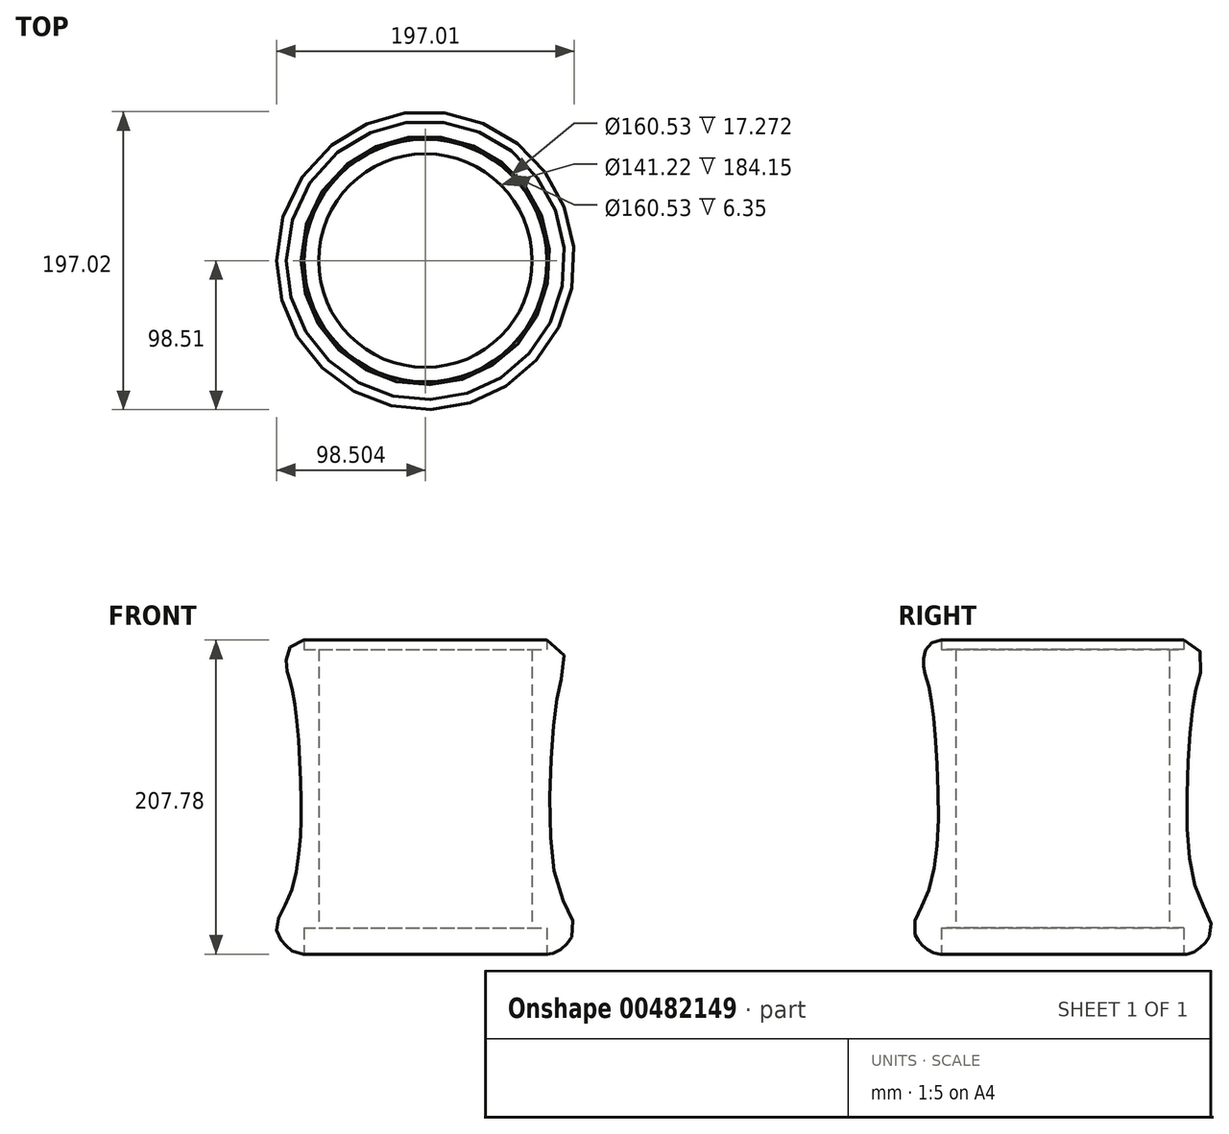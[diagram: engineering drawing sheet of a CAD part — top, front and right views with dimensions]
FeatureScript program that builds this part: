
annotation { "Feature Type Name" : "Feature", "Feature Type Description" : "" }
export const myFeature = defineFeature(function(context is Context, id is Id, definition is map)
    precondition{}
    {
        {
            var Q0;
            Q0=qCreatedBy(makeId("Front.planeOp"),FACE);
            var sketch = newSketch(context, id + "F0", { "sketchPlane" : qUnion([Q0])});
            skLineSegment(sketch, "E0", {"start": v(-86.64, -88.91) * mm, "end": v(-76.99, -88.91) * mm});
            skLineSegment(sketch, "E1", {"start": v(-76.99, -88.91) * mm, "end": v(-76.99, 95.24) * mm});
            skLineSegment(sketch, "E2", {"start": v(-76.99, 95.24) * mm, "end": v(-86.64, 95.24) * mm});
            skLineSegment(sketch, "E3", {"start": v(-86.64, 95.24) * mm, "end": v(-86.64, 101.59) * mm});
            skLineSegment(sketch, "E4", {"start": v(-86.64, -88.91) * mm, "end": v(-86.64, -106.19) * mm});
            skFitSpline(sketch, "E5", {"points": [v(-86.64, 101.59) * mm, v(-98.44, 87.66) * mm, v(-96.55, 76.7) * mm, v(-93.9, 65.72) * mm, v(-90.44, 36.31) * mm, v(-88.6, -4.63) * mm, v(-89.74, -36.78) * mm, v(-96.55, -68.55) * mm, v(-104.87, -88.22) * mm, v(-101.09, -98.06) * mm, v(-96.93, -102.22) * mm, v(-86.64, -106.19) * mm], "startDerivative": vector(-322.63, -18.4) * mm, "endDerivative": vector(246.37, 6.49) * mm});
            skLineSegment(sketch, "E6", {"start": v(-76.99, -88.91) * mm, "end": v(-6.38, -88.91) * mm, "construction": true});
            skLineSegment(sketch, "E7", {"start": v(-6.38, -88.91) * mm, "end": v(-6.38, 139.69) * mm, "construction": true});
            skLineSegment(sketch, "E8", {"start": v(-6.38, -88.91) * mm, "end": v(-6.38, -106.19) * mm, "construction": true});
            skSolve(sketch);
        }
        {
            var Q0;
            Q0=makeQuery(id+"F0.imprint","IMPRINT",FACE,{"disambiguationData":[TD([[makeQuery(id+"F0.imprint","IMPRINT",EDGE,{"derivedFrom":sQuery(id+"F0.wireOp",EDGE,"E0")}),1.0]])]});
            var Q1;
            Q1=sQuery(id+"F0.wireOp",EDGE,"E7");
            revolve(context, id + "F1", {"entities" : qUnion([Q0]), "axis" : qUnion([Q1]), "revolveType" : RevolveType.FULL});
        }
    });
